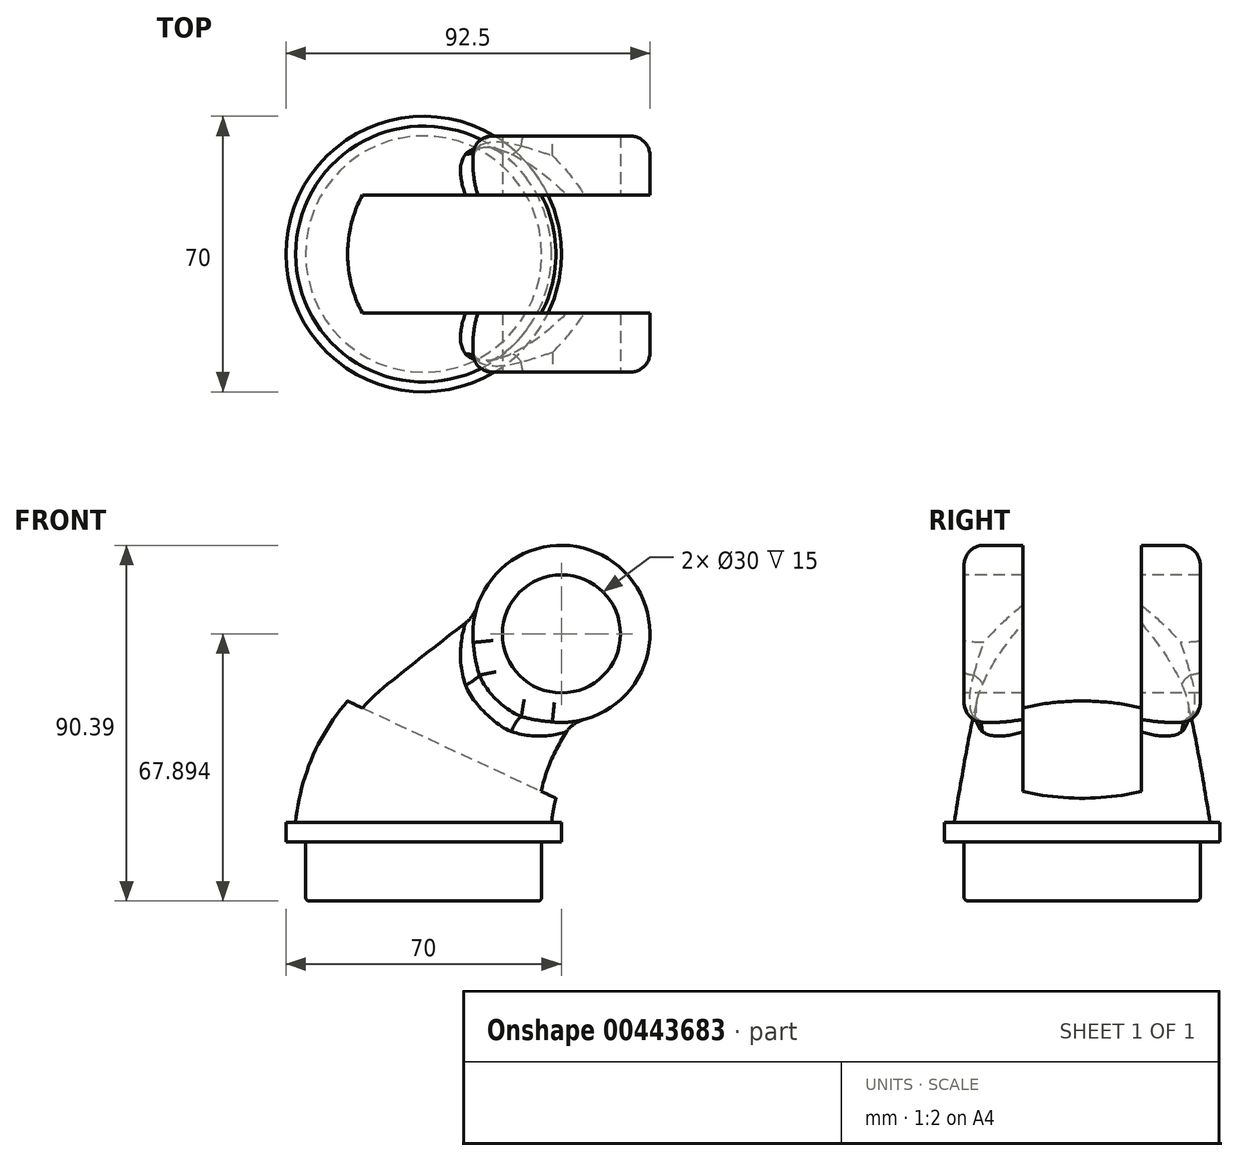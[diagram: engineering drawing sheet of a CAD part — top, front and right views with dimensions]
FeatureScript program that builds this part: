
annotation { "Feature Type Name" : "Feature", "Feature Type Description" : "" }
export const myFeature = defineFeature(function(context is Context, id is Id, definition is map)
    precondition{}
    {
        {
            var Q0;
            Q0=qCreatedBy(makeId("Top.planeOp"),FACE);
            var sketch = newSketch(context, id + "F0", { "sketchPlane" : qUnion([Q0])});
            skCircle(sketch, "E0", {"center": v(0, 0) * mm, "radius": 35 * mm});
            skSolve(sketch);
        }
        {
            var Q0;
            Q0=makeQuery(id+"F0.imprint","IMPRINT",FACE,{"disambiguationData":[TD([[makeQuery(id+"F0.imprint","IMPRINT",EDGE,{"derivedFrom":sQuery(id+"F0.wireOp",EDGE,"E0")}),1.0]])]});
            extrude(context, id + "F1", {"entities" : qUnion([Q0]), "depth" : 5 * mm});
        }
        {
            var Q0;
            Q0=qCreatedBy(makeId("Front.planeOp"),FACE);
            var sketch = newSketch(context, id + "F2", { "sketchPlane" : qUnion([Q0])});
            skArc(sketch, "E1", {"start": v(17.6, 38.3) * mm, "mid": v(5.55, 23.37) * mm, "end": v(0, 5) * mm});
            skLineSegment(sketch, "E2", {"start": v(17.6, 38.3) * mm, "end": v(35, 52.9) * mm});
            skSolve(sketch);
        }
        {
            var Q0;
            Q0=sQuery(id+"F2.wireOp",EDGE,"E2");
            var Q1;
            Q1=sQuery(id+"F2.wireOp",VERTEX,"E2.end");
            cPlane(context, id + "F3", {"entities" : qUnion([Q0, Q1]), "cplaneType" : CPlaneType.LINE_POINT, "offset" : 25 * mm, "width" : 150 * mm, "height" : 150 * mm});
        }
        {
            var Q0;
            Q0=qCreatedBy(id+"F3.planeOp",FACE);
            var sketch = newSketch(context, id + "F4", { "sketchPlane" : qUnion([Q0])});
            skCircle(sketch, "E3", {"center": v(0, 18.02) * mm, "radius": 22.5 * mm});
            skSolve(sketch);
        }
        {
            var Q0;
            Q0=makeQuery(id+"F1.opExtrude","CAP_FACE",FACE,{"disambiguationData":[OSD([sQuery(id+"F0.wireOp",EDGE,"E0")])],"isStart":false});
            var sketch = newSketch(context, id + "F5", { "sketchPlane" : qUnion([Q0])});
            skCircle(sketch, "E4", {"center": v(0, 0) * mm, "radius": 32.5 * mm});
            skSolve(sketch);
        }
        {
            var Q0;
            Q0=qCreatedBy(makeId("Front.planeOp"),FACE);
            var sketch = newSketch(context, id + "F6", { "sketchPlane" : qUnion([Q0])});
            skArc(sketch, "E5", {"start": v(-13.25, 41.78) * mm, "mid": v(-26.5, 25.3) * mm, "end": v(-32.5, 5) * mm});
            skLineSegment(sketch, "E6", {"start": v(-13.25, 41.78) * mm, "end": v(20.54, 70.13) * mm});
            skSolve(sketch);
        }
        {
            var Q0;
            Q0=qCreatedBy(makeId("Front.planeOp"),FACE);
            var sketch = newSketch(context, id + "F7", { "sketchPlane" : qUnion([Q0])});
            skArc(sketch, "E7", {"start": v(48.46, 34.82) * mm, "mid": v(37.6, 21.45) * mm, "end": v(32.5, 5) * mm});
            skLineSegment(sketch, "E8", {"start": v(48.46, 34.82) * mm, "end": v(49.46, 35.66) * mm});
            skSolve(sketch);
        }
        {
            var Q1;
            Q1=makeQuery(id+"F4.imprint","IMPRINT",FACE,{"disambiguationData":[TD([[makeQuery(id+"F4.imprint","IMPRINT",EDGE,{"derivedFrom":sQuery(id+"F4.wireOp",EDGE,"E3")}),1.0]])]});
            var Q2;
            Q2=makeQuery(id+"F5.imprint","IMPRINT",FACE,{"disambiguationData":[TD([[makeQuery(id+"F5.imprint","IMPRINT",EDGE,{"derivedFrom":sQuery(id+"F5.wireOp",EDGE,"E4")}),1.0]])]});
            var Q3;
            Q3 = qConstructionFilter(qBodyType(qCreatedBy(id + "F6" ,EDGE), BodyType.WIRE), ConstructionObject.NO);
            var Q4;
            Q4 = qConstructionFilter(qBodyType(qCreatedBy(id + "F7" ,EDGE), BodyType.WIRE), ConstructionObject.NO);
            loft(context, id + "F8", {"operationType" : NewBodyOperationType.ADD, "addGuides" : true, "sheetProfilesArray" : [{ "sheetProfileEntities" : qUnion([Q1]) }, { "sheetProfileEntities" : qUnion([Q2]) }], "guidesArray" : [{ "guideEntities" : qUnion([Q3]), "guideDerivativeType" : LoftGuideDerivativeType.DEFAULT, "guideDerivativeMagnitude" : 1 }, { "guideEntities" : qUnion([Q4]), "guideDerivativeType" : LoftGuideDerivativeType.DEFAULT, "guideDerivativeMagnitude" : 1 }]});
        }
        {
            var Q0;
            Q0=qCreatedBy(makeId("Front.planeOp"),FACE);
            var sketch = newSketch(context, id + "F9", { "sketchPlane" : qUnion([Q0])});
            skCircle(sketch, "E9", {"center": v(35, 52.9) * mm, "radius": 22.5 * mm});
            skSolve(sketch);
        }
        {
            var Q0;
            Q0 = qSketchRegion(id + "F9", true);
            extrude(context, id + "F10", {"entities" : qUnion([Q0]), "operationType" : NewBodyOperationType.ADD, "endBound" : BoundingType.SYMMETRIC, "depth" : 60 * mm});
        }
        {
            var Q0;
            Q0=makeQuery(id+"F10.boolean.opBoolean","INTERSECT",EDGE,{"disambiguationData":[OD(1.0)],"derivedFrom":[makeQuery(id+"F8.opLoft","SWEPT_FACE",FACE,{"disambiguationData":[OSD([sQuery(id+"F4.wireOp",EDGE,"E3"),sQuery(id+"F5.wireOp",EDGE,"E4"),sQuery(id+"F6.wireOp",VERTEX,"E6.start"),sQuery(id+"F6.wireOp",EDGE,"E5"),sQuery(id+"F6.wireOp",EDGE,"E6"),sQuery(id+"F7.wireOp",VERTEX,"E8.start"),sQuery(id+"F7.wireOp",EDGE,"E7"),sQuery(id+"F7.wireOp",EDGE,"E8")])]}),makeQuery(id+"F10.opExtrude","SWEPT_FACE",FACE,{"disambiguationData":[OSD([sQuery(id+"F9.wireOp",EDGE,"E9")])]})]});
            var Q1;
            Q1=makeQuery(id+"F10.boolean.opBoolean","INTERSECT",EDGE,{"disambiguationData":[OD(0.0)],"derivedFrom":[makeQuery(id+"F8.opLoft","SWEPT_FACE",FACE,{"disambiguationData":[OSD([sQuery(id+"F4.wireOp",EDGE,"E3"),sQuery(id+"F5.wireOp",EDGE,"E4"),sQuery(id+"F6.wireOp",VERTEX,"E6.start"),sQuery(id+"F6.wireOp",EDGE,"E5"),sQuery(id+"F6.wireOp",EDGE,"E6"),sQuery(id+"F7.wireOp",VERTEX,"E8.start"),sQuery(id+"F7.wireOp",EDGE,"E7"),sQuery(id+"F7.wireOp",EDGE,"E8")])]}),makeQuery(id+"F10.opExtrude","SWEPT_FACE",FACE,{"disambiguationData":[OSD([sQuery(id+"F9.wireOp",EDGE,"E9")])]})]});
            fillet(context, id + "F11", {"entities" : qUnion([Q0, Q1]), "radius" : 5 * mm, "tangentPropagation" : true, "allowEdgeOverflow" : false});
        }
        {
            var Q0;
            Q0=makeQuery(id+"F10.opExtrude","CAP_FACE",FACE,{"disambiguationData":[OSD([sQuery(id+"F9.wireOp",EDGE,"E9")])],"isStart":false});
            var Q1;
            Q1=makeQuery(id+"F10.opExtrude","CAP_FACE",FACE,{"disambiguationData":[OSD([sQuery(id+"F9.wireOp",EDGE,"E9")])],"isStart":true});
            fillet(context, id + "F12", {"entities" : qUnion([Q0, Q1]), "radius" : 5 * mm, "tangentPropagation" : true, "allowEdgeOverflow" : false});
        }
        {
            var Q0;
            Q0=makeQuery(id+"F10.opExtrude","CAP_FACE",FACE,{"disambiguationData":[OSD([sQuery(id+"F9.wireOp",EDGE,"E9")])],"isStart":false});
            var sketch = newSketch(context, id + "F13", { "sketchPlane" : qUnion([Q0])});
            skCircle(sketch, "E10", {"center": v(35, 52.9) * mm, "radius": 15 * mm});
            skSolve(sketch);
        }
        {
            var Q0;
            Q0=makeQuery(id+"F13.imprint","IMPRINT",FACE,{"disambiguationData":[TD([[makeQuery(id+"F13.imprint","IMPRINT",EDGE,{"derivedFrom":sQuery(id+"F13.wireOp",EDGE,"E10")}),1.0]])]});
            extrude(context, id + "F14", {"entities" : qUnion([Q0]), "operationType" : NewBodyOperationType.REMOVE, "endBound" : BoundingType.THROUGH_ALL, "oppositeDirection" : true, "depth" : 25 * mm});
        }
        {
            var Q0;
            Q0=qCreatedBy(makeId("Front.planeOp"),FACE);
            var sketch = newSketch(context, id + "F15", { "sketchPlane" : qUnion([Q0])});
            skLineSegment(sketch, "E11", {"start": v(-104.18, 75.4) * mm, "end": v(57.5, 0) * mm});
            skLineSegment(sketch, "E12", {"start": v(57.5, 75.4) * mm, "end": v(57.5, 0) * mm});
            skLineSegment(sketch, "E13", {"start": v(57.5, 75.4) * mm, "end": v(-104.18, 75.4) * mm});
            skSolve(sketch);
        }
        {
            var Q0;
            Q0=makeQuery(id+"F15.imprint","IMPRINT",FACE,{"disambiguationData":[TD([[makeQuery(id+"F15.imprint","IMPRINT",EDGE,{"derivedFrom":sQuery(id+"F15.wireOp",EDGE,"E11")}),1.0]])]});
            extrude(context, id + "F16", {"entities" : qUnion([Q0]), "operationType" : NewBodyOperationType.REMOVE, "endBound" : BoundingType.SYMMETRIC, "oppositeDirection" : true, "depth" : 30 * mm});
        }
        {
            var Q0;
            Q0=qCreatedBy(makeId("Front.planeOp"),FACE);
            var sketch = newSketch(context, id + "F17", { "sketchPlane" : qUnion([Q0])});
            skLineSegment(sketch, "E14.bottom", {"start": v(0, 0) * mm, "end": v(-30, 0) * mm});
            skLineSegment(sketch, "E14.top", {"start": v(0, -15) * mm, "end": v(-30, -15) * mm});
            skLineSegment(sketch, "E14.left", {"start": v(0, 0) * mm, "end": v(0, -15) * mm});
            skLineSegment(sketch, "E14.right", {"start": v(-30, 0) * mm, "end": v(-30, -15) * mm});
            skSolve(sketch);
        }
        {
            var Q0;
            Q0=makeQuery(id+"F17.imprint","IMPRINT",FACE,{"disambiguationData":[TD([[makeQuery(id+"F17.imprint","IMPRINT",EDGE,{"derivedFrom":sQuery(id+"F17.wireOp",EDGE,"E14.bottom")}),1.0]])]});
            var Q1;
            Q1=sQuery(id+"F17.wireOp",EDGE,"E14.left");
            revolve(context, id + "F18", {"operationType" : NewBodyOperationType.ADD, "entities" : qUnion([Q0]), "axis" : qUnion([Q1]), "revolveType" : RevolveType.FULL});
        }
        {
            var Q0;
            Q0=makeQuery(id+"F18.opRevolve","SWEPT_EDGE",EDGE,{"disambiguationData":[OSD([sQuery(id+"F17.wireOp",EDGE,"E14.top"),sQuery(id+"F17.wireOp",EDGE,"E14.right")])]});
            var Q1;
            Q1=makeQuery(id+"F18.opRevolve","SWEPT_EDGE",EDGE,{"disambiguationData":[OSD([sQuery(id+"F17.wireOp",EDGE,"E14.bottom"),sQuery(id+"F17.wireOp",EDGE,"E14.right")])]});
            fillet(context, id + "F19", {"entities" : qUnion([Q0, Q1]), "radius" : 1 * mm, "tangentPropagation" : true, "allowEdgeOverflow" : false});
        }
    });
